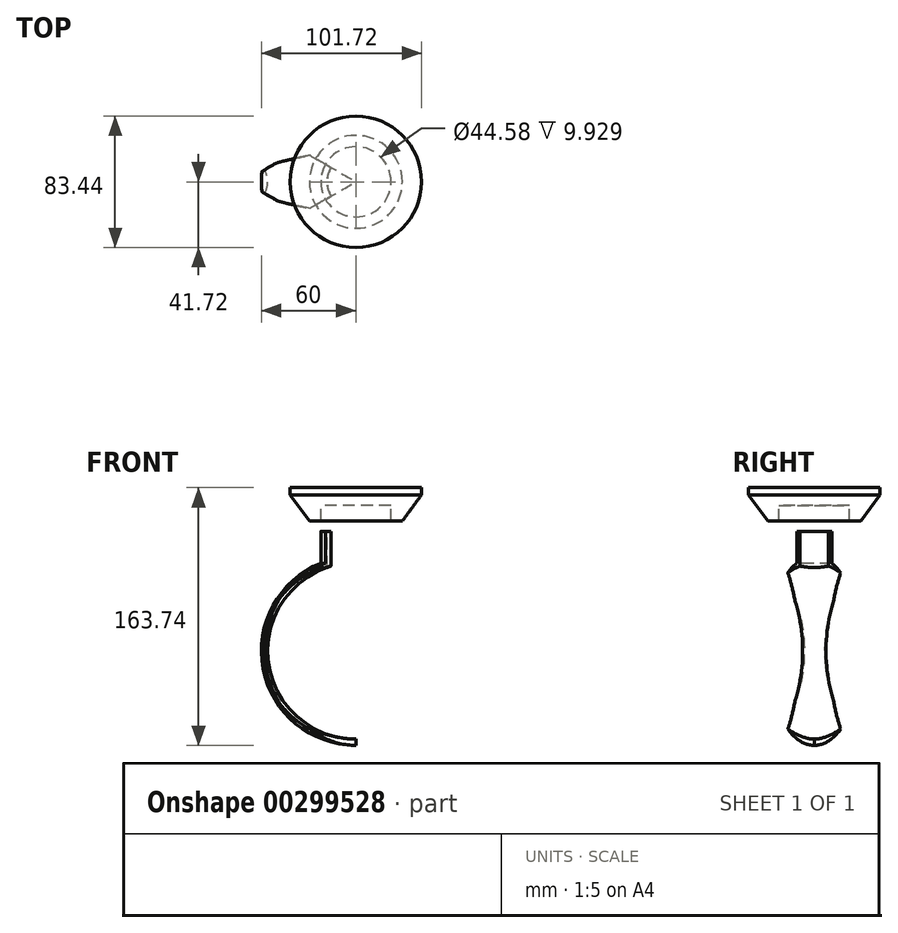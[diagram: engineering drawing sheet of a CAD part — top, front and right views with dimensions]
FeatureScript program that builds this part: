
annotation { "Feature Type Name" : "Feature", "Feature Type Description" : "" }
export const myFeature = defineFeature(function(context is Context, id is Id, definition is map)
    precondition{}
    {
        {
            var Q0;
            Q0=qCreatedBy(makeId("Front.planeOp"),FACE);
            var sketch = newSketch(context, id + "F0", { "sketchPlane" : qUnion([Q0])});
            skLineSegment(sketch, "E0.top", {"start": v(0, -88.74) * mm, "end": v(70.7, -88.74) * mm});
            skLineSegment(sketch, "E0.left", {"start": v(0, 75.06) * mm, "end": v(0, -88.74) * mm});
            skLineSegment(sketch, "E0.right", {"start": v(70.7, 75.06) * mm, "end": v(70.7, -88.74) * mm});
            skArc(sketch, "E1", {"start": v(70.7, 55.16) * mm, "mid": v(14.7, -0.84) * mm, "end": v(70.7, -56.84) * mm});
            skArc(sketch, "E2", {"start": v(48.41, 54.87) * mm, "mid": v(11.78, -12.19) * mm, "end": v(70.7, -60.84) * mm});
            skLineSegment(sketch, "E3", {"start": v(0, 75.06) * mm, "end": v(70.7, 75.06) * mm});
            skLineSegment(sketch, "E4", {"start": v(48.41, 75.06) * mm, "end": v(48.41, 54.87) * mm});
            skLineSegment(sketch, "E5", {"start": v(48.41, 54.87) * mm, "end": v(48.41, 108.47) * mm, "construction": true});
            skLineSegment(sketch, "E6", {"start": v(70.7, 75.06) * mm, "end": v(70.7, 111.44) * mm, "construction": true});
            skLineSegment(sketch, "E7", {"start": v(48.41, 81.67) * mm, "end": v(48.41, 91.6) * mm});
            skLineSegment(sketch, "E8", {"start": v(48.41, 91.6) * mm, "end": v(70.7, 91.6) * mm});
            skLineSegment(sketch, "E9", {"start": v(70.7, 91.6) * mm, "end": v(70.7, 98.27) * mm});
            skLineSegment(sketch, "E10", {"start": v(48.41, 81.67) * mm, "end": v(41.2, 81.67) * mm});
            skLineSegment(sketch, "E11", {"start": v(41.2, 81.67) * mm, "end": v(28.98, 98.27) * mm});
            skLineSegment(sketch, "E12", {"start": v(28.98, 98.27) * mm, "end": v(28.98, 102.9) * mm});
            skLineSegment(sketch, "E13", {"start": v(28.98, 102.9) * mm, "end": v(70.7, 102.9) * mm});
            skLineSegment(sketch, "E14", {"start": v(70.7, 102.9) * mm, "end": v(70.7, 98.27) * mm});
            skSolve(sketch);
        }
        {
            var Q0;
            {var subQ1=sQuery(id+"F0.wireOp",EDGE,"E1");Q0=makeQuery(id+"F0.imprint","IMPRINT",FACE,{"disambiguationData":[TD([[makeQuery(id+"F0.imprint","IMPRINT",EDGE,{"derivedFrom":subQ1}),-1.0]])]});}
            var Q1;
            Q1=sQuery(id+"F0.wireOp",EDGE,"E0.right");
            revolve(context, id + "F1", {"surfaceOperationType" : NewSurfaceOperationType.NEW, "entities" : qUnion([Q0]), "axis" : qUnion([Q1]), "revolveType" : RevolveType.SYMMETRIC, "angle" : 60 * degree});
        }
        {
            var Q0;
            {var subQ0=sQuery(id+"F0.wireOp",EDGE,"E1");Q0=makeQuery(id+"F0.imprint","IMPRINT",FACE,{"disambiguationData":[TD([[makeQuery(id+"F0.imprint","IMPRINT",EDGE,{"derivedFrom":subQ0}),1.0]])]});}
            var Q1;
            Q1=sQuery(id+"F0.wireOp",EDGE,"E0.left");
            revolve(context, id + "F2", {"operationType" : NewBodyOperationType.REMOVE, "surfaceOperationType" : NewSurfaceOperationType.NEW, "entities" : qUnion([Q0]), "axis" : qUnion([Q1]), "revolveType" : RevolveType.SYMMETRIC, "angle" : 180 * degree});
        }
        {
            var Q0;
            Q0=makeQuery(id+"F1.opRevolve","SWEPT_FACE",FACE,{"disambiguationData":[OSD([sQuery(id+"F0.wireOp",EDGE,"E3")])]});
            var sketch = newSketch(context, id + "F3", { "sketchPlane" : qUnion([Q0])});
            skCircle(sketch, "E15", {"center": v(70.7, 0) * mm, "radius": 18.22 * mm});
            skLineSegment(sketch, "E16", {"start": v(70.7, 0) * mm, "end": v(35.77, -20.65) * mm});
            skLineSegment(sketch, "E17", {"start": v(70.7, 0) * mm, "end": v(34.93, 20.65) * mm});
            skLineSegment(sketch, "E18", {"start": v(0, 0) * mm, "end": v(35.77, -20.65) * mm});
            skPoint(sketch, "E19.orphan", {"position": v(0, -41.8) * mm});
            skLineSegment(sketch, "E20", {"start": v(0, 0) * mm, "end": v(34.93, 20.65) * mm});
            skPoint(sketch, "E21.start.orphan", {"position": v(0, 40.82) * mm});
            skLineSegment(sketch, "E22", {"start": v(34.93, 20.65) * mm, "end": v(0, 40.82) * mm});
            skLineSegment(sketch, "E23", {"start": v(0, -41.8) * mm, "end": v(35.77, -20.65) * mm});
            skLineSegment(sketch, "E24", {"start": v(0, -41.8) * mm, "end": v(0, 40.82) * mm});
            skSolve(sketch);
        }
        {
            var Q0;
            {var subQ0=sQuery(id+"F3.wireOp",EDGE,"E15");var subQ1=sQuery(id+"F0.wireOp",EDGE,"E3");var subQ2=makeQuery(id+"F1.opRevolve","CAP_EDGE",EDGE,{"disambiguationData":[OSD([subQ1])],"isStart":true});var subQ3=makeQuery(id+"F3.imprint","INTERSECT",VERTEX,{"derivedFrom":[subQ2,subQ0]});Q0=makeQuery(id+"F3.imprint","IMPRINT",FACE,{"disambiguationData":[TD([[makeQuery(id+"F3.imprint","IMPRINT",EDGE,{"disambiguationData":[TD([[subQ3,1.0]])],"derivedFrom":subQ0}),1.0]])]});}
            extrude(context, id + "F4", {"entities" : qUnion([Q0]), "operationType" : NewBodyOperationType.REMOVE, "oppositeDirection" : true, "depth" : 25 * mm, "offsetDistance" : 25 * mm});
        }
        {
            var Q0;
            Q0=makeQuery(id+"F0.imprint","IMPRINT",FACE,{"disambiguationData":[TD([[makeQuery(id+"F0.imprint","IMPRINT",EDGE,{"derivedFrom":sQuery(id+"F0.wireOp",EDGE,"E7")}),1.0]])]});
            var Q1;
            Q1=sQuery(id+"F0.wireOp",EDGE,"E0.right");
            revolve(context, id + "F5", {"surfaceOperationType" : NewSurfaceOperationType.NEW, "entities" : qUnion([Q0]), "axis" : qUnion([Q1]), "revolveType" : RevolveType.FULL});
        }
        {
            var Q0;
            {var subQ0=sQuery(id+"F3.wireOp",EDGE,"E18");Q0=makeQuery(id+"F3.imprint","IMPRINT",FACE,{"disambiguationData":[TD([[makeQuery(id+"F3.imprint","IMPRINT",EDGE,{"derivedFrom":subQ0}),-1.0]])]});}
            extrude(context, id + "F6", {"entities" : qUnion([Q0]), "operationType" : NewBodyOperationType.REMOVE, "oppositeDirection" : true, "depth" : 136.7 * mm, "offsetDistance" : 25 * mm});
        }
        {
            var Q0;
            {var subQ0=sQuery(id+"F3.wireOp",EDGE,"E20");Q0=makeQuery(id+"F3.imprint","IMPRINT",FACE,{"disambiguationData":[TD([[makeQuery(id+"F3.imprint","IMPRINT",EDGE,{"derivedFrom":subQ0}),1.0]])]});}
            extrude(context, id + "F7", {"entities" : qUnion([Q0]), "operationType" : NewBodyOperationType.REMOVE, "oppositeDirection" : true, "depth" : 138.9 * mm, "offsetDistance" : 25 * mm});
        }
    });
